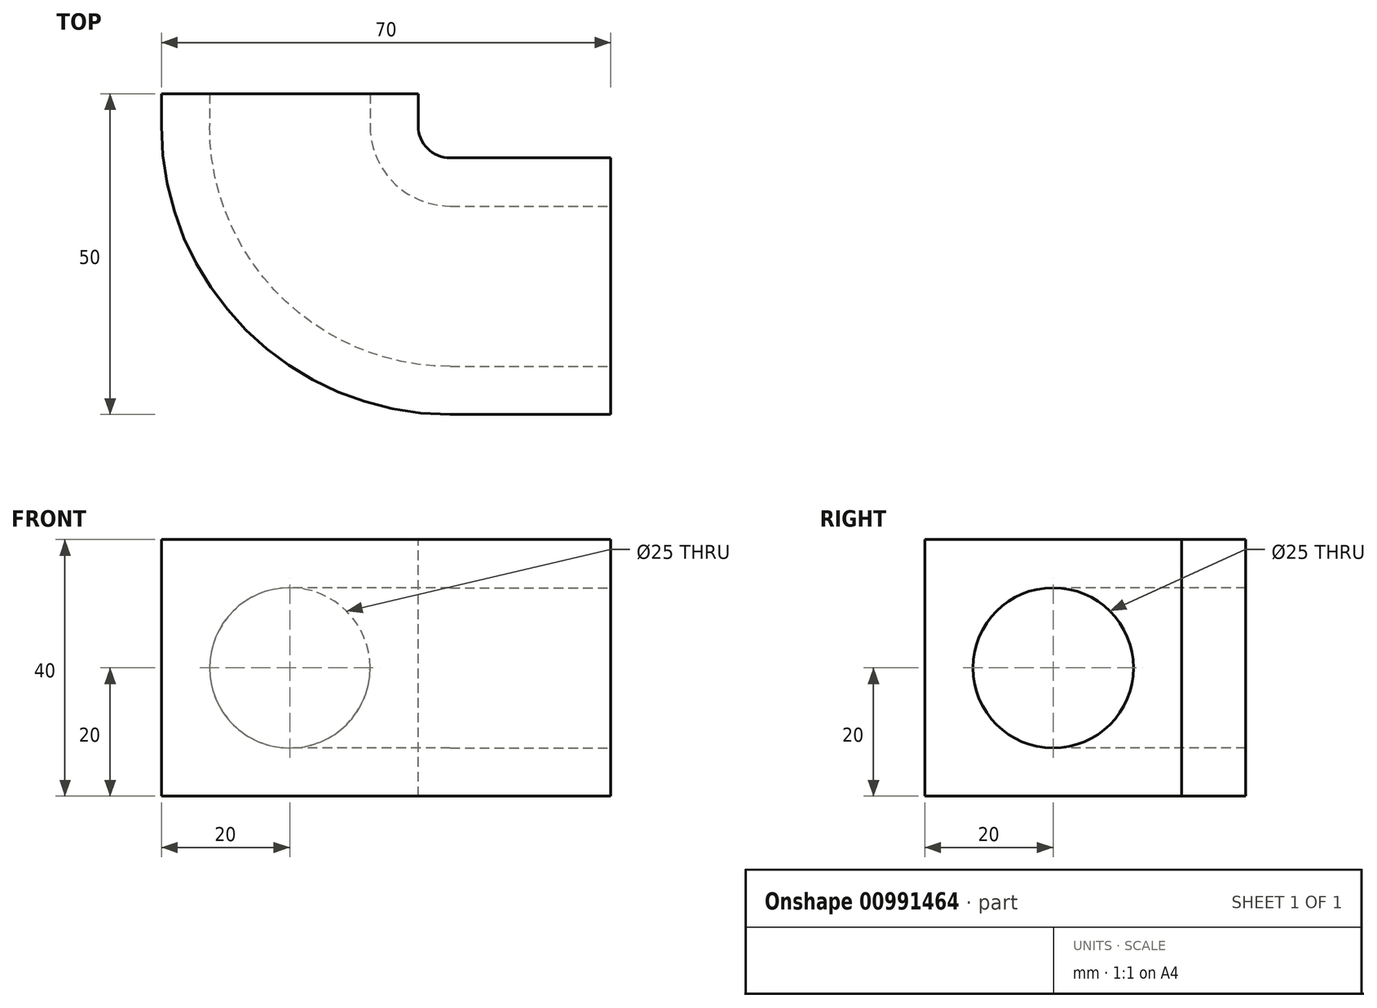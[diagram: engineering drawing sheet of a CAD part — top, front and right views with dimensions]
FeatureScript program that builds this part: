
annotation { "Feature Type Name" : "Feature", "Feature Type Description" : "" }
export const myFeature = defineFeature(function(context is Context, id is Id, definition is map)
    precondition{}
    {
        {
            var Q0;
            Q0=qCreatedBy(makeId("Top.planeOp"),FACE);
            var sketch = newSketch(context, id + "F0", { "sketchPlane" : qUnion([Q0])});
            skCircle(sketch, "E0", {"center": v(0, 0) * mm, "radius": 12.5 * mm});
            skLineSegment(sketch, "E1.bottom", {"start": v(-20, -20) * mm, "end": v(20, -20) * mm});
            skLineSegment(sketch, "E1.top", {"start": v(-20, 20) * mm, "end": v(20, 20) * mm});
            skLineSegment(sketch, "E1.left", {"start": v(-20, -20) * mm, "end": v(-20, 20) * mm});
            skLineSegment(sketch, "E1.right", {"start": v(20, -20) * mm, "end": v(20, 20) * mm});
            skSolve(sketch);
        }
        {
            var Q0;
            Q0=qCreatedBy(makeId("Front.planeOp"),FACE);
            var sketch = newSketch(context, id + "F1", { "sketchPlane" : qUnion([Q0])});
            skLineSegment(sketch, "E2", {"start": v(0, 0) * mm, "end": v(0, 5) * mm});
            skLineSegment(sketch, "E3", {"start": v(25, 30) * mm, "end": v(50, 30) * mm});
            skPoint(sketch, "E4.visualSharp", {"position": v(0, 30) * mm});
            skArc(sketch, "E4.filletArc", {"start": v(25, 30) * mm, "mid": v(7.32, 22.68) * mm, "end": v(0, 5) * mm});
            skSolve(sketch);
        }
        {
            var Q0;
            Q0=makeQuery(id+"F0.imprint","IMPRINT",FACE,{"disambiguationData":[TD([[makeQuery(id+"F0.imprint","IMPRINT",EDGE,{"derivedFrom":sQuery(id+"F0.wireOp",EDGE,"E0")}),-1.0]])]});
            var Q1;
            Q1=sQuery(id+"F1.wireOp",EDGE,"E2");
            var Q2;
            Q2=sQuery(id+"F1.wireOp",EDGE,"E4.filletArc");
            var Q3;
            Q3=sQuery(id+"F1.wireOp",EDGE,"E3");
            sweep(context, id + "F2", {"profiles" : qUnion([Q0]), "path" : qUnion([Q1, Q2, Q3])});
        }
        {
            var Q0;
            Q0=makeQuery(id+"F2.opSweep","SWEPT_BODY",BODY,{"disambiguationData":[OSD([sQuery(id+"F0.wireOp",EDGE,"E0"),sQuery(id+"F0.wireOp",EDGE,"E1.bottom"),sQuery(id+"F0.wireOp",EDGE,"E1.top"),sQuery(id+"F0.wireOp",EDGE,"E1.left"),sQuery(id+"F0.wireOp",EDGE,"E1.right"),sQuery(id+"F1.wireOp",EDGE,"E3")])]});
            var Q1;
            Q1=makeQuery(id+"F2.opSweep","CAP_EDGE",EDGE,{"disambiguationData":[OSD([sQuery(id+"F0.wireOp",EDGE,"E1.bottom"),sQuery(id+"F1.wireOp",VERTEX,"E2.start")])],"isStart":true});
            var Q2;
            Q2=makeQuery(id+"F2.opSweep","CAP_EDGE",EDGE,{"disambiguationData":[OSD([sQuery(id+"F0.wireOp",EDGE,"E1.bottom"),sQuery(id+"F1.wireOp",VERTEX,"E2.start")])],"isStart":true});
            transform(context, id + "F3", {"entities" : qUnion([Q0]), "transformType" : TransformType.ROTATION, "transformAxis" : qUnion([Q2]), "angle" : 90 * degree, "makeCopy" : false});
        }
    });
